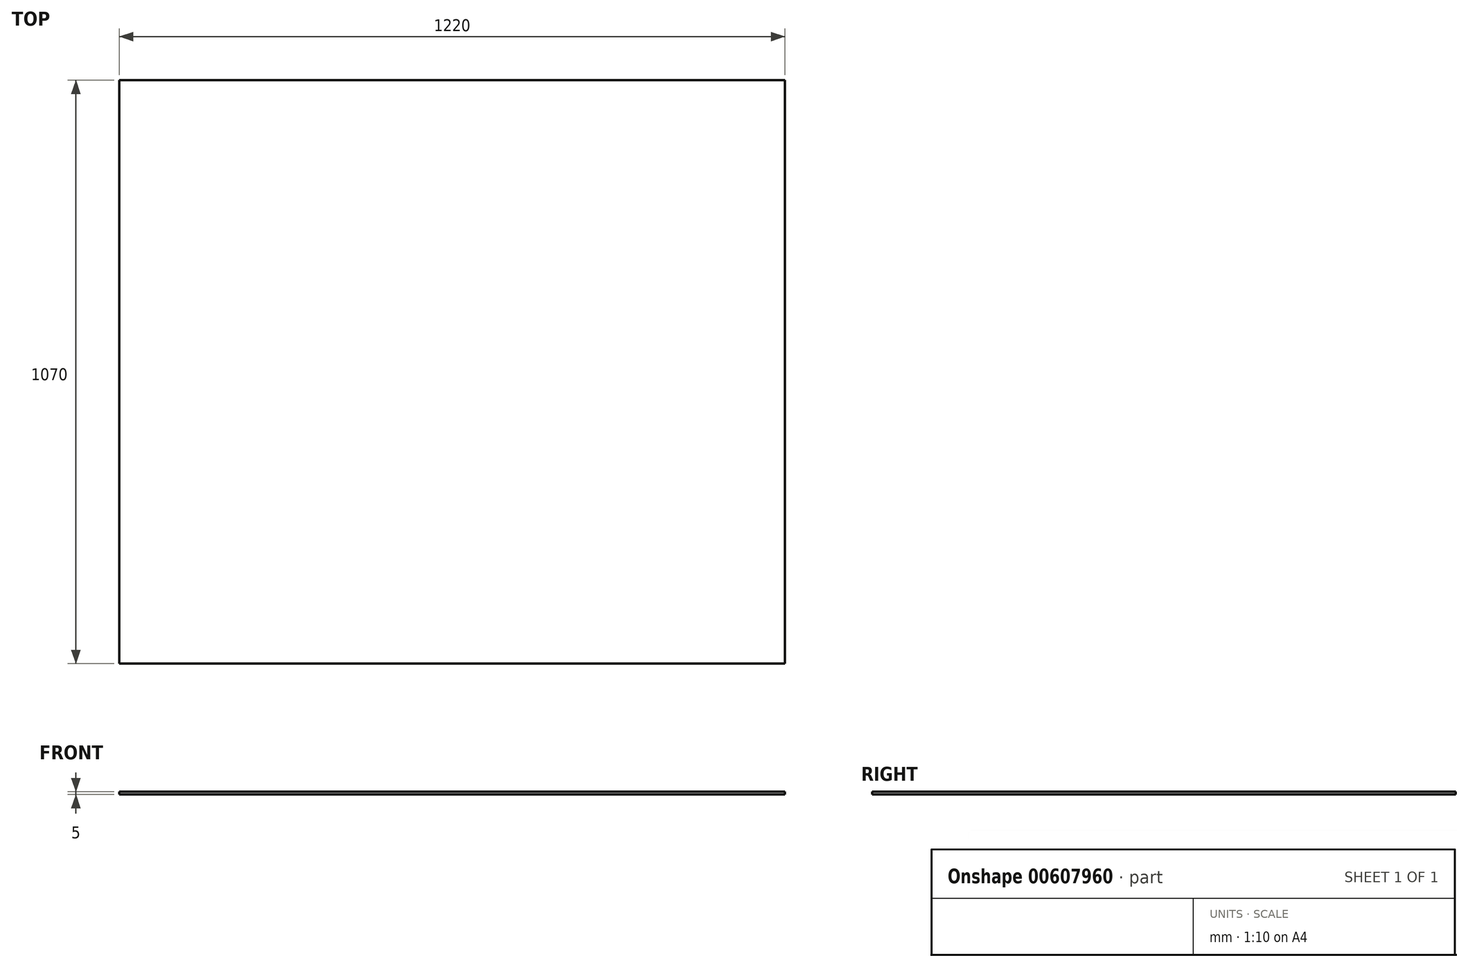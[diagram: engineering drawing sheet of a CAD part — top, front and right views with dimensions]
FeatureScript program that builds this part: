
annotation { "Feature Type Name" : "Feature", "Feature Type Description" : "" }
export const myFeature = defineFeature(function(context is Context, id is Id, definition is map)
    precondition{}
    {
        {
            var Q0;
            Q0=qCreatedBy(makeId("Front.planeOp"),FACE);
            var sketch = newSketch(context, id + "F0", { "sketchPlane" : qUnion([Q0])});
            skLineSegment(sketch, "E0.bottom", {"start": v(-61.2, 5) * mm, "end": v(1158.8, 5) * mm});
            skLineSegment(sketch, "E0.top", {"start": v(-61.2, 0) * mm, "end": v(1158.8, 0) * mm});
            skLineSegment(sketch, "E0.left", {"start": v(-61.2, 5) * mm, "end": v(-61.2, 0) * mm});
            skLineSegment(sketch, "E0.right", {"start": v(1158.8, 5) * mm, "end": v(1158.8, 0) * mm});
            skSolve(sketch);
        }
        {
            var Q0;
            Q0 = qSketchRegion(id + "F0", true);
            extrude(context, id + "F1", {"entities" : qUnion([Q0]), "depth" : 535 * mm, "offsetDistance" : 25 * mm, "hasSecondDirection" : true, "secondDirectionOppositeDirection" : true, "secondDirectionDepth" : 535 * mm});
        }
    });
